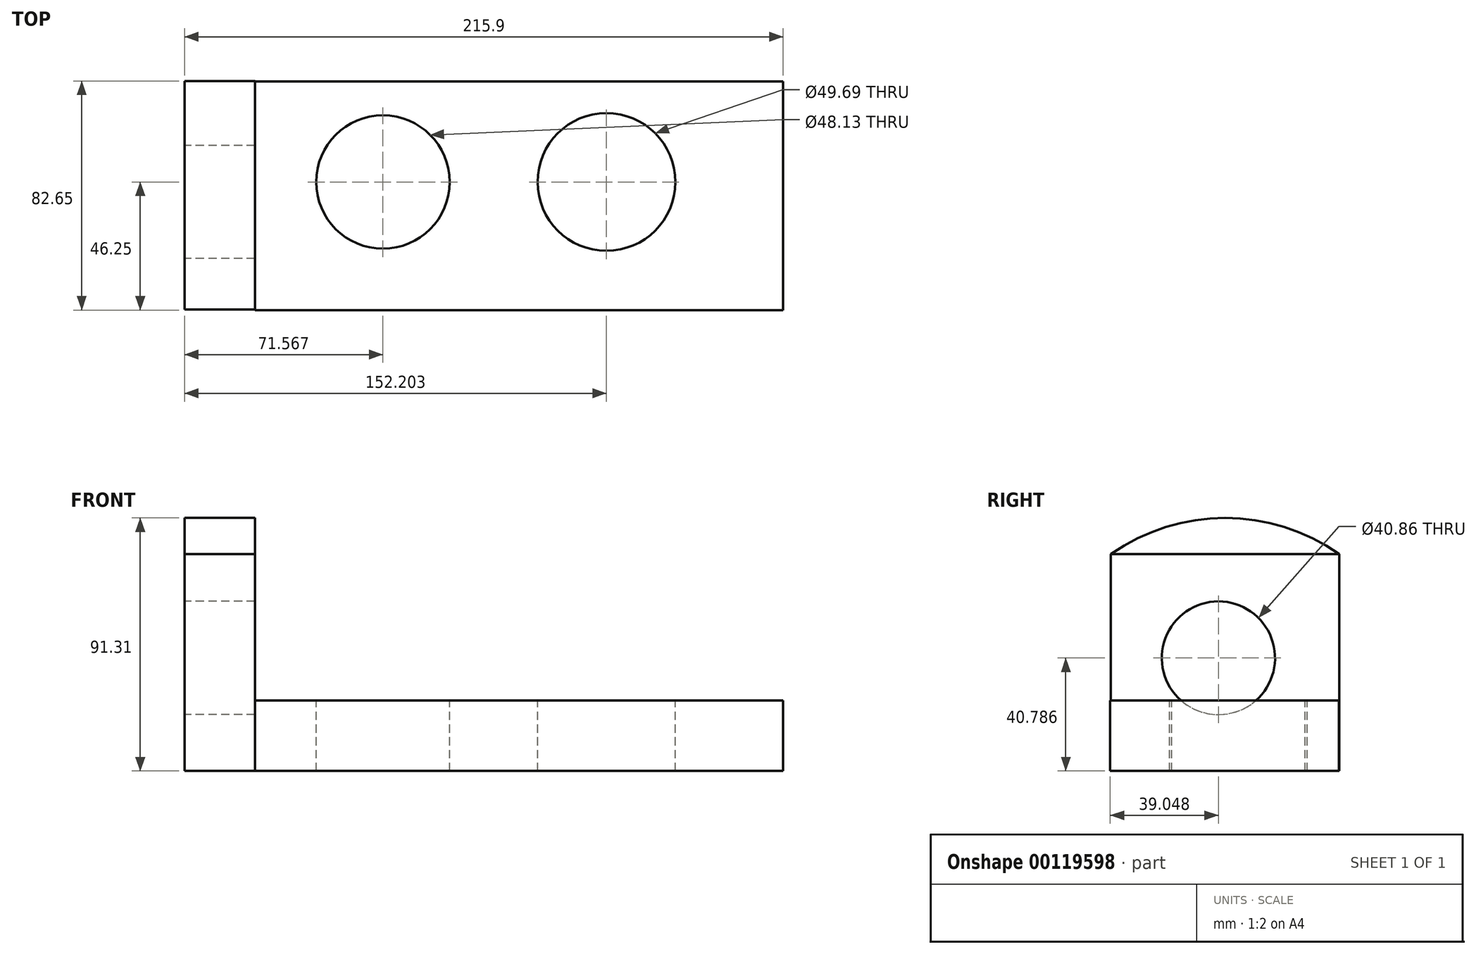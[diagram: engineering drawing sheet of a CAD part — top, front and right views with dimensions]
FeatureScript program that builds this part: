
annotation { "Feature Type Name" : "Feature", "Feature Type Description" : "" }
export const myFeature = defineFeature(function(context is Context, id is Id, definition is map)
    precondition{}
    {
        {
            var Q0;
            Q0=qCreatedBy(makeId("Top.planeOp"),FACE);
            var sketch = newSketch(context, id + "F0", { "sketchPlane" : qUnion([Q0])});
            skLineSegment(sketch, "E0.bottom", {"start": v(-70.87, 36.3) * mm, "end": v(119.63, 36.3) * mm});
            skLineSegment(sketch, "E0.top", {"start": v(-70.87, -46.25) * mm, "end": v(119.63, -46.25) * mm});
            skLineSegment(sketch, "E0.left", {"start": v(-70.87, 36.3) * mm, "end": v(-70.87, -46.25) * mm});
            skLineSegment(sketch, "E0.right", {"start": v(119.63, 36.3) * mm, "end": v(119.63, -46.25) * mm});
            skSolve(sketch);
        }
        {
            var Q0;
            Q0 = qSketchRegion(id + "F0", true);
            extrude(context, id + "F1", {"entities" : qUnion([Q0]), "depth" : 25.4 * mm});
        }
        {
            var Q0;
            Q0=makeQuery(id+"F1.opExtrude","CAP_FACE",FACE,{"disambiguationData":[OSD([sQuery(id+"F0.wireOp",EDGE,"E0.bottom"),sQuery(id+"F0.wireOp",EDGE,"E0.top"),sQuery(id+"F0.wireOp",EDGE,"E0.left"),sQuery(id+"F0.wireOp",EDGE,"E0.right")])],"isStart":false});
            var sketch = newSketch(context, id + "F2", { "sketchPlane" : qUnion([Q0])});
            skCircle(sketch, "E1", {"center": v(-24.7, 0) * mm, "radius": 24.07 * mm});
            skCircle(sketch, "E2", {"center": v(55.93, 0) * mm, "radius": 24.84 * mm});
            skSolve(sketch);
        }
        {
            var Q0;
            Q0 = qSketchRegion(id + "F2", true);
            extrude(context, id + "F3", {"entities" : qUnion([Q0]), "operationType" : NewBodyOperationType.REMOVE, "oppositeDirection" : true, "depth" : 25.4 * mm});
        }
        {
            var Q0;
            Q0=makeQuery(id+"F1.opExtrude","SWEPT_FACE",FACE,{"disambiguationData":[OSD([sQuery(id+"F0.wireOp",EDGE,"E0.left")])]});
            var sketch = newSketch(context, id + "F4", { "sketchPlane" : qUnion([Q0])});
            skLineSegment(sketch, "E3.bottom", {"start": v(-36.4, 0) * mm, "end": v(46, 0) * mm});
            skLineSegment(sketch, "E3.top", {"start": v(-36.4, 78.23) * mm, "end": v(46, 78.23) * mm});
            skLineSegment(sketch, "E3.left", {"start": v(-36.4, 0) * mm, "end": v(-36.4, 78.23) * mm});
            skLineSegment(sketch, "E3.right", {"start": v(46, 0) * mm, "end": v(46, 78.23) * mm});
            skArc(sketch, "E4", {"start": v(46, 78.23) * mm, "mid": v(4.8, 91.3) * mm, "end": v(-36.4, 78.23) * mm});
            skSolve(sketch);
        }
        {
            var Q0;
            Q0=makeQuery(id+"F4.imprint","IMPRINT",FACE,{"disambiguationData":[TD([[makeQuery(id+"F4.imprint","IMPRINT",EDGE,{"derivedFrom":sQuery(id+"F4.wireOp",EDGE,"E3.top")}),1.0]])]});
            extrude(context, id + "F5", {"entities" : qUnion([Q0]), "depth" : 25.4 * mm});
        }
        {
            var Q0;
            Q0 = qSketchRegion(id + "F4", true);
            extrude(context, id + "F6", {"entities" : qUnion([Q0]), "depth" : 25.4 * mm});
        }
        {
            var Q0;
            Q0=makeQuery(id+"F6.opExtrude","CAP_FACE",FACE,{"disambiguationData":[OSD([sQuery(id+"F4.wireOp",EDGE,"E3.bottom"),sQuery(id+"F4.wireOp",EDGE,"E3.left"),sQuery(id+"F4.wireOp",EDGE,"E3.right"),sQuery(id+"F4.wireOp",EDGE,"E4")])],"isStart":false});
            var sketch = newSketch(context, id + "F7", { "sketchPlane" : qUnion([Q0])});
            skCircle(sketch, "E5", {"center": v(7.2, 40.79) * mm, "radius": 20.43 * mm});
            skSolve(sketch);
        }
        {
            var Q0;
            Q0 = qSketchRegion(id + "F7", true);
            extrude(context, id + "F8", {"entities" : qUnion([Q0]), "operationType" : NewBodyOperationType.REMOVE, "oppositeDirection" : true, "depth" : 25.4 * mm});
        }
    });
